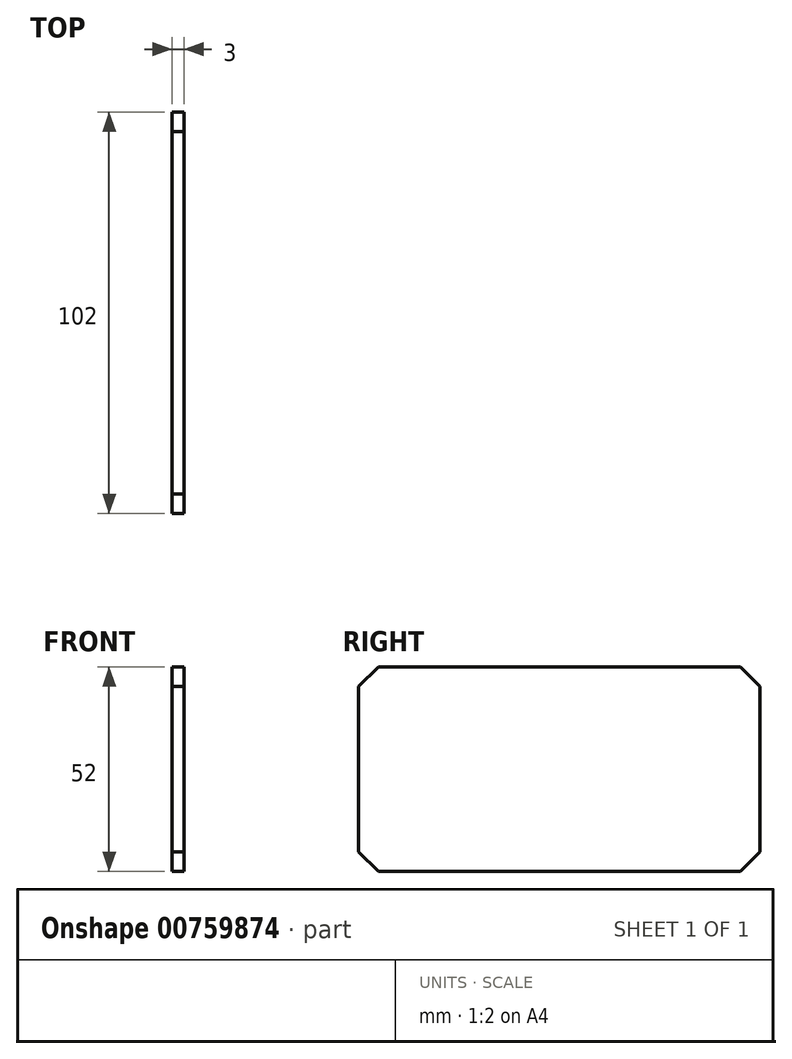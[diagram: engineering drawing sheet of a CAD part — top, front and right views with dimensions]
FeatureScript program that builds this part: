
annotation { "Feature Type Name" : "Feature", "Feature Type Description" : "" }
export const myFeature = defineFeature(function(context is Context, id is Id, definition is map)
    precondition{}
    {
        {
            var Q0;
            Q0=qCreatedBy(makeId("Right.planeOp"),FACE);
            var sketch = newSketch(context, id + "F0", { "sketchPlane" : qUnion([Q0])});
            skLineSegment(sketch, "E0.bottom", {"start": v(51, 26) * mm, "end": v(-51, 26) * mm});
            skLineSegment(sketch, "E0.top", {"start": v(51, -26) * mm, "end": v(-51, -26) * mm});
            skLineSegment(sketch, "E0.left", {"start": v(51, 26) * mm, "end": v(51, -26) * mm});
            skLineSegment(sketch, "E0.right", {"start": v(-51, 26) * mm, "end": v(-51, -26) * mm});
            skPoint(sketch, "E0.middle", {"position": v(0, 0) * mm});
            skSolve(sketch);
        }
        {
            var Q0;
            Q0=makeQuery(id+"F0.imprint","IMPRINT",FACE,{"disambiguationData":[TD([[makeQuery(id+"F0.imprint","IMPRINT",EDGE,{"derivedFrom":sQuery(id+"F0.wireOp",EDGE,"E0.bottom")}),1.0]])]});
            extrude(context, id + "F1", {"entities" : qUnion([Q0]), "depth" : 3 * mm, "offsetDistance" : 25 * mm});
        }
        {
            var Q0;
            Q0=makeQuery(id+"F1.opExtrude","SWEPT_EDGE",EDGE,{"disambiguationData":[OSD([sQuery(id+"F0.wireOp",EDGE,"E0.bottom"),sQuery(id+"F0.wireOp",EDGE,"E0.right")])]});
            var Q1;
            Q1=makeQuery(id+"F1.opExtrude","SWEPT_EDGE",EDGE,{"disambiguationData":[OSD([sQuery(id+"F0.wireOp",EDGE,"E0.top"),sQuery(id+"F0.wireOp",EDGE,"E0.right")])]});
            var Q2;
            Q2=makeQuery(id+"F1.opExtrude","SWEPT_EDGE",EDGE,{"disambiguationData":[OSD([sQuery(id+"F0.wireOp",EDGE,"E0.bottom"),sQuery(id+"F0.wireOp",EDGE,"E0.left")])]});
            var Q3;
            Q3=makeQuery(id+"F1.opExtrude","SWEPT_EDGE",EDGE,{"disambiguationData":[OSD([sQuery(id+"F0.wireOp",EDGE,"E0.top"),sQuery(id+"F0.wireOp",EDGE,"E0.left")])]});
            chamfer(context, id + "F2", {"entities" : qUnion([Q0, Q1, Q2, Q3]), "width" : 5 * mm, "tangentPropagation" : true});
        }
    });
